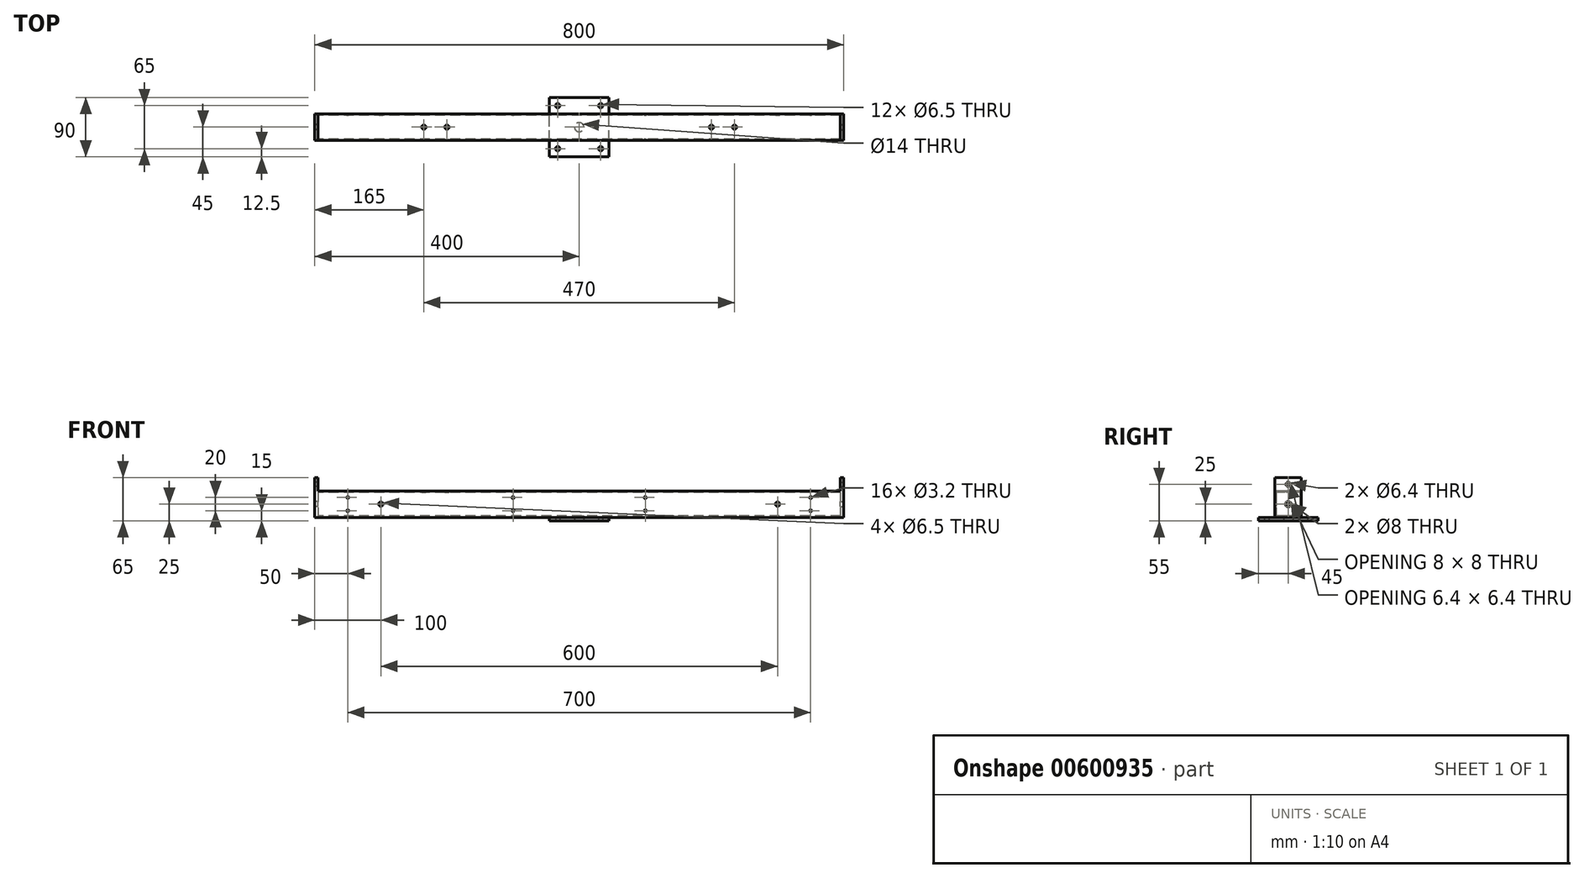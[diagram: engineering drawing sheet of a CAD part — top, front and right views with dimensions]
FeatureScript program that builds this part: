
annotation { "Feature Type Name" : "Feature", "Feature Type Description" : "" }
export const myFeature = defineFeature(function(context is Context, id is Id, definition is map)
    precondition{}
    {
        {
            var Q0;
            Q0=qCreatedBy(makeId("Right.planeOp"),FACE);
            var sketch = newSketch(context, id + "F0", { "sketchPlane" : qUnion([Q0])});
            skLineSegment(sketch, "E0.bottom", {"start": v(20, 20) * mm, "end": v(-20, 20) * mm});
            skLineSegment(sketch, "E0.top", {"start": v(20, -20) * mm, "end": v(-20, -20) * mm});
            skLineSegment(sketch, "E0.left", {"start": v(20, 20) * mm, "end": v(20, -20) * mm});
            skLineSegment(sketch, "E0.right", {"start": v(-20, 20) * mm, "end": v(-20, -20) * mm});
            skPoint(sketch, "E0.middle", {"position": v(0, 0) * mm});
            skLineSegment(sketch, "E1.bottom", {"start": v(18, 18) * mm, "end": v(-18, 18) * mm});
            skLineSegment(sketch, "E1.top", {"start": v(18, -18) * mm, "end": v(-18, -18) * mm});
            skLineSegment(sketch, "E1.left", {"start": v(18, 18) * mm, "end": v(18, -18) * mm});
            skLineSegment(sketch, "E1.right", {"start": v(-18, 18) * mm, "end": v(-18, -18) * mm});
            skSolve(sketch);
        }
        {
            var Q0;
            Q0=makeQuery(id+"F0.imprint","IMPRINT",FACE,{"disambiguationData":[TD([[makeQuery(id+"F0.imprint","IMPRINT",EDGE,{"derivedFrom":sQuery(id+"F0.wireOp",EDGE,"E0.bottom")}),1.0]])]});
            extrude(context, id + "F1", {"entities" : qUnion([Q0]), "depth" : 400 * mm, "offsetDistance" : 25 * mm});
        }
        {
            var Q0;
            Q0=qCreatedBy(makeId("Right.planeOp"),FACE);
            var sketch = newSketch(context, id + "F2", { "sketchPlane" : qUnion([Q0])});
            skLineSegment(sketch, "E2.bottom", {"start": v(20, -20) * mm, "end": v(-20, -20) * mm});
            skLineSegment(sketch, "E2.top", {"start": v(20, 40) * mm, "end": v(-20, 40) * mm});
            skLineSegment(sketch, "E2.left", {"start": v(20, -20) * mm, "end": v(20, 40) * mm});
            skLineSegment(sketch, "E2.right", {"start": v(-20, -20) * mm, "end": v(-20, 40) * mm});
            skPoint(sketch, "E3", {"position": v(0, 30) * mm});
            skPoint(sketch, "E4", {"position": v(0, 0) * mm});
            skSolve(sketch);
        }
        {
            var Q0;
            Q0=makeQuery(id+"F2.imprint","IMPRINT",FACE,{"disambiguationData":[TD([[makeQuery(id+"F2.imprint","IMPRINT",EDGE,{"derivedFrom":sQuery(id+"F2.wireOp",EDGE,"E2.bottom")}),-1.0]])]});
            extrude(context, id + "F3", {"entities" : qUnion([Q0]), "operationType" : NewBodyOperationType.ADD, "depth" : 5 * mm, "offsetDistance" : 25 * mm});
        }
        {
            var Q0;
            Q0=sQuery(id+"F2.wireOp",VERTEX,"E3");
            var Q1;
            Q1=makeQuery(id+"F1.opExtrude","SWEPT_BODY",BODY,{"disambiguationData":[OSD([sQuery(id+"F0.wireOp",EDGE,"E0.bottom"),sQuery(id+"F0.wireOp",EDGE,"E0.top"),sQuery(id+"F0.wireOp",EDGE,"E0.left"),sQuery(id+"F0.wireOp",EDGE,"E0.right"),sQuery(id+"F0.wireOp",EDGE,"E1.bottom"),sQuery(id+"F0.wireOp",EDGE,"E1.top"),sQuery(id+"F0.wireOp",EDGE,"E1.left"),sQuery(id+"F0.wireOp",EDGE,"E1.right")])]});
            hole(context, id + "F4", {"style" : HoleStyle.SIMPLE, "endStyle" : HoleEndStyle.THROUGH, "oppositeDirection" : true, "standardTappedOrClearance" : lookupTablePath({ "standard" : "ISO", "size" : "6.4", "type" : "Drilled" }), "standardBlindInLast" : lookupTablePath({ "standard" : "ISO", "size" : "6.4", "type" : "Drilled" }), "holeDiameter" : 6.4 * mm, "isTappedThrough" : true, "tappedDepth" : 3.5 * mm, "tapClearance" : 3, "locations" : qUnion([Q0]), "scope" : qUnion([Q1])});
        }
        {
            var Q0;
            Q0=makeQuery(id+"F1.opExtrude","SWEPT_FACE",FACE,{"disambiguationData":[OSD([sQuery(id+"F0.wireOp",EDGE,"E0.bottom")])]});
            var sketch = newSketch(context, id + "F5", { "sketchPlane" : qUnion([Q0])});
            skPoint(sketch, "E5", {"position": v(200, 0) * mm});
            skPoint(sketch, "E6", {"position": v(165, 0) * mm});
            skSolve(sketch);
        }
        {
            var Q0;
            Q0=sQuery(id+"F5.wireOp",VERTEX,"E6");
            var Q1;
            Q1=sQuery(id+"F5.wireOp",VERTEX,"E5");
            var Q2;
            Q2=makeQuery(id+"F1.opExtrude","SWEPT_BODY",BODY,{"disambiguationData":[OSD([sQuery(id+"F0.wireOp",EDGE,"E0.bottom"),sQuery(id+"F0.wireOp",EDGE,"E0.top"),sQuery(id+"F0.wireOp",EDGE,"E0.left"),sQuery(id+"F0.wireOp",EDGE,"E0.right"),sQuery(id+"F0.wireOp",EDGE,"E1.bottom"),sQuery(id+"F0.wireOp",EDGE,"E1.top"),sQuery(id+"F0.wireOp",EDGE,"E1.left"),sQuery(id+"F0.wireOp",EDGE,"E1.right")])]});
            hole(context, id + "F6", {"style" : HoleStyle.SIMPLE, "endStyle" : HoleEndStyle.THROUGH, "standardTappedOrClearance" : lookupTablePath({ "standard" : "ISO", "size" : "6.5", "type" : "Drilled" }), "standardBlindInLast" : lookupTablePath({ "standard" : "ISO", "size" : "6.5", "type" : "Drilled" }), "holeDiameter" : 6.5 * mm, "isTappedThrough" : true, "tappedDepth" : 3.5 * mm, "tapClearance" : 3, "locations" : qUnion([Q0, Q1]), "scope" : qUnion([Q2])});
        }
        {
            var Q0;
            Q0=makeQuery(id+"F3.boolean.opBoolean","MERGE",FACE,{"derivedFrom":[makeQuery(id+"F1.opExtrude","SWEPT_FACE",FACE,{"disambiguationData":[OSD([sQuery(id+"F0.wireOp",EDGE,"E0.right")])]}),makeQuery(id+"F3.opExtrude","SWEPT_FACE",FACE,{"disambiguationData":[OSD([sQuery(id+"F2.wireOp",EDGE,"E2.right")])]})]});
            var sketch = newSketch(context, id + "F7", { "sketchPlane" : qUnion([Q0])});
            skPoint(sketch, "E7", {"position": v(50, 10) * mm});
            skPoint(sketch, "E8", {"position": v(50, -10) * mm});
            skPoint(sketch, "E9", {"position": v(300, 10) * mm});
            skPoint(sketch, "E10", {"position": v(300, -10) * mm});
            skPoint(sketch, "E11", {"position": v(100, 0) * mm});
            skSolve(sketch);
        }
        {
            var Q0;
            Q0=sQuery(id+"F7.wireOp",VERTEX,"E7");
            var Q1;
            Q1=sQuery(id+"F7.wireOp",VERTEX,"E8");
            var Q2;
            Q2=sQuery(id+"F7.wireOp",VERTEX,"E9");
            var Q3;
            Q3=sQuery(id+"F7.wireOp",VERTEX,"E10");
            var Q4;
            Q4=makeQuery(id+"F1.opExtrude","SWEPT_BODY",BODY,{"disambiguationData":[OSD([sQuery(id+"F0.wireOp",EDGE,"E0.bottom"),sQuery(id+"F0.wireOp",EDGE,"E0.top"),sQuery(id+"F0.wireOp",EDGE,"E0.left"),sQuery(id+"F0.wireOp",EDGE,"E0.right"),sQuery(id+"F0.wireOp",EDGE,"E1.bottom"),sQuery(id+"F0.wireOp",EDGE,"E1.top"),sQuery(id+"F0.wireOp",EDGE,"E1.left"),sQuery(id+"F0.wireOp",EDGE,"E1.right")])]});
            hole(context, id + "F8", {"style" : HoleStyle.SIMPLE, "endStyle" : HoleEndStyle.THROUGH, "standardTappedOrClearance" : lookupTablePath({ "standard" : "ISO", "size" : "3.2", "type" : "Drilled" }), "standardBlindInLast" : lookupTablePath({ "standard" : "ISO", "size" : "3.2", "type" : "Drilled" }), "holeDiameter" : 3.2 * mm, "isTappedThrough" : true, "tappedDepth" : 3.5 * mm, "tapClearance" : 3, "locations" : qUnion([Q0, Q1, Q2, Q3]), "scope" : qUnion([Q4])});
        }
        {
            var Q0;
            Q0=sQuery(id+"F2.wireOp",VERTEX,"E4");
            var Q1;
            Q1=makeQuery(id+"F1.opExtrude","SWEPT_BODY",BODY,{"disambiguationData":[OSD([sQuery(id+"F0.wireOp",EDGE,"E0.bottom"),sQuery(id+"F0.wireOp",EDGE,"E0.top"),sQuery(id+"F0.wireOp",EDGE,"E0.left"),sQuery(id+"F0.wireOp",EDGE,"E0.right"),sQuery(id+"F0.wireOp",EDGE,"E1.bottom"),sQuery(id+"F0.wireOp",EDGE,"E1.top"),sQuery(id+"F0.wireOp",EDGE,"E1.left"),sQuery(id+"F0.wireOp",EDGE,"E1.right")])]});
            hole(context, id + "F9", {"style" : HoleStyle.SIMPLE, "endStyle" : HoleEndStyle.THROUGH, "oppositeDirection" : true, "standardTappedOrClearance" : lookupTablePath({ "standard" : "ISO", "size" : "8", "type" : "Drilled" }), "standardBlindInLast" : lookupTablePath({ "standard" : "ISO", "size" : "8", "type" : "Drilled" }), "holeDiameter" : 8 * mm, "isTappedThrough" : true, "tappedDepth" : 3.5 * mm, "tapClearance" : 3, "locations" : qUnion([Q0]), "scope" : qUnion([Q1])});
        }
        {
            var Q0;
            Q0=sQuery(id+"F7.wireOp",VERTEX,"E11");
            var Q1;
            Q1=makeQuery(id+"F1.opExtrude","SWEPT_BODY",BODY,{"disambiguationData":[OSD([sQuery(id+"F0.wireOp",EDGE,"E0.bottom"),sQuery(id+"F0.wireOp",EDGE,"E0.top"),sQuery(id+"F0.wireOp",EDGE,"E0.left"),sQuery(id+"F0.wireOp",EDGE,"E0.right"),sQuery(id+"F0.wireOp",EDGE,"E1.bottom"),sQuery(id+"F0.wireOp",EDGE,"E1.top"),sQuery(id+"F0.wireOp",EDGE,"E1.left"),sQuery(id+"F0.wireOp",EDGE,"E1.right")])]});
            hole(context, id + "F10", {"style" : HoleStyle.SIMPLE, "endStyle" : HoleEndStyle.THROUGH, "standardTappedOrClearance" : lookupTablePath({ "standard" : "ISO", "size" : "6.5", "type" : "Drilled" }), "standardBlindInLast" : lookupTablePath({ "standard" : "ISO", "size" : "6.5", "type" : "Drilled" }), "holeDiameter" : 6.5 * mm, "isTappedThrough" : true, "tappedDepth" : 3.5 * mm, "tapClearance" : 3, "locations" : qUnion([Q0]), "scope" : qUnion([Q1])});
        }
        {
            var Q0;
            Q0=makeQuery(id+"F1.opExtrude","CAP_FACE",FACE,{"disambiguationData":[OSD([sQuery(id+"F0.wireOp",EDGE,"E0.bottom"),sQuery(id+"F0.wireOp",EDGE,"E0.top"),sQuery(id+"F0.wireOp",EDGE,"E0.left"),sQuery(id+"F0.wireOp",EDGE,"E0.right"),sQuery(id+"F0.wireOp",EDGE,"E1.bottom"),sQuery(id+"F0.wireOp",EDGE,"E1.top"),sQuery(id+"F0.wireOp",EDGE,"E1.left"),sQuery(id+"F0.wireOp",EDGE,"E1.right")])],"isStart":false});
            var sketch = newSketch(context, id + "F11", { "sketchPlane" : qUnion([Q0])});
            skSolve(sketch);
        }
        {
            var Q0;
            Q0=makeQuery(id+"F1.opExtrude","SWEPT_BODY",BODY,{"disambiguationData":[OSD([sQuery(id+"F0.wireOp",EDGE,"E0.bottom"),sQuery(id+"F0.wireOp",EDGE,"E0.top"),sQuery(id+"F0.wireOp",EDGE,"E0.left"),sQuery(id+"F0.wireOp",EDGE,"E0.right"),sQuery(id+"F0.wireOp",EDGE,"E1.bottom"),sQuery(id+"F0.wireOp",EDGE,"E1.top"),sQuery(id+"F0.wireOp",EDGE,"E1.left"),sQuery(id+"F0.wireOp",EDGE,"E1.right")])]});
            var Q1;
            Q1=makeQuery(id+"F11.imprint","IMPRINT",FACE,{"disambiguationData":[TD([[makeQuery(id+"F11.imprint","IMPRINT",EDGE,{"derivedFrom":makeQuery(id+"F1.opExtrude","CAP_EDGE",EDGE,{"disambiguationData":[OSD([sQuery(id+"F0.wireOp",EDGE,"E0.bottom")])],"isStart":false})}),1.0]])]});
            mirror(context, id + "F12", {"operationType" : NewBodyOperationType.ADD, "entities" : qUnion([Q0]), "mirrorPlane" : qUnion([Q1])});
        }
        {
            var Q0;
            {var subQ0=makeQuery(id+"F1.opExtrude","SWEPT_FACE",FACE,{"disambiguationData":[OSD([sQuery(id+"F0.wireOp",EDGE,"E0.top")])]});Q0=makeQuery(id+"F12.boolean.opBoolean","MERGE",FACE,{"derivedFrom":[subQ0,makeQuery(id+"F12.opPattern","COPY",FACE,{"derivedFrom":subQ0,"instanceName":"1"})]});}
            var sketch = newSketch(context, id + "F13", { "sketchPlane" : qUnion([Q0])});
            skLineSegment(sketch, "E12.bottom", {"start": v(355, 45) * mm, "end": v(445, 45) * mm});
            skLineSegment(sketch, "E12.top", {"start": v(355, -45) * mm, "end": v(445, -45) * mm});
            skLineSegment(sketch, "E12.left", {"start": v(355, 45) * mm, "end": v(355, -45) * mm});
            skLineSegment(sketch, "E12.right", {"start": v(445, 45) * mm, "end": v(445, -45) * mm});
            skSolve(sketch);
        }
        {
            var Q0;
            {var subQ0=sQuery(id+"F13.wireOp",EDGE,"E12.bottom");Q0=makeQuery(id+"F13.imprint","IMPRINT",FACE,{"disambiguationData":[TD([[makeQuery(id+"F13.imprint","IMPRINT",EDGE,{"derivedFrom":subQ0}),-1.0]])]});}
            var Q1;
            {var subQ0=sQuery(id+"F13.wireOp",EDGE,"E12.top");Q1=makeQuery(id+"F13.imprint","IMPRINT",FACE,{"disambiguationData":[TD([[makeQuery(id+"F13.imprint","IMPRINT",EDGE,{"derivedFrom":subQ0}),1.0]])]});}
            var Q2;
            {var subQ0=sQuery(id+"F13.wireOp",EDGE,"E12.left");var subQ1=sQuery(id+"F0.wireOp",EDGE,"E0.top");var subQ2=makeQuery(id+"F1.opExtrude","SWEPT_EDGE",EDGE,{"disambiguationData":[OSD([subQ1,sQuery(id+"F0.wireOp",EDGE,"E0.right")])]});var subQ3=makeQuery(id+"F12.boolean.opBoolean","MERGE",EDGE,{"derivedFrom":[subQ2,makeQuery(id+"F12.opPattern","COPY",EDGE,{"derivedFrom":subQ2,"instanceName":"1"})]});var subQ4=makeQuery(id+"F13.imprint","INTERSECT",VERTEX,{"derivedFrom":[subQ3,subQ0]});Q2=makeQuery(id+"F13.imprint","IMPRINT",FACE,{"disambiguationData":[TD([[makeQuery(id+"F13.imprint","IMPRINT",EDGE,{"disambiguationData":[TD([[subQ4,-1.0]])],"derivedFrom":subQ0}),1.0]])]});}
            extrude(context, id + "F14", {"entities" : qUnion([Q0, Q1, Q2]), "operationType" : NewBodyOperationType.ADD, "depth" : 5 * mm, "offsetDistance" : 25 * mm});
        }
        {
            var Q0;
            Q0=makeQuery(id+"F14.opExtrude","CAP_FACE",FACE,{"disambiguationData":[OSD([sQuery(id+"F13.wireOp",EDGE,"E12.bottom"),sQuery(id+"F13.wireOp",EDGE,"E12.top"),sQuery(id+"F13.wireOp",EDGE,"E12.left"),sQuery(id+"F13.wireOp",EDGE,"E12.right")])],"isStart":false});
            var sketch = newSketch(context, id + "F15", { "sketchPlane" : qUnion([Q0])});
            skPoint(sketch, "E13", {"position": v(367.5, 32.5) * mm});
            skPoint(sketch, "E14", {"position": v(432.5, 32.5) * mm});
            skPoint(sketch, "E15", {"position": v(432.5, -32.5) * mm});
            skPoint(sketch, "E16", {"position": v(367.5, -32.5) * mm});
            skPoint(sketch, "E17", {"position": v(400, 0) * mm});
            skSolve(sketch);
        }
        {
            var Q0;
            Q0=sQuery(id+"F15.wireOp",VERTEX,"E13");
            var Q1;
            Q1=sQuery(id+"F15.wireOp",VERTEX,"E14");
            var Q2;
            Q2=sQuery(id+"F15.wireOp",VERTEX,"E15");
            var Q3;
            Q3=sQuery(id+"F15.wireOp",VERTEX,"E16");
            var Q4;
            Q4=makeQuery(id+"F1.opExtrude","SWEPT_BODY",BODY,{"disambiguationData":[OSD([sQuery(id+"F0.wireOp",EDGE,"E0.bottom"),sQuery(id+"F0.wireOp",EDGE,"E0.top"),sQuery(id+"F0.wireOp",EDGE,"E0.left"),sQuery(id+"F0.wireOp",EDGE,"E0.right"),sQuery(id+"F0.wireOp",EDGE,"E1.bottom"),sQuery(id+"F0.wireOp",EDGE,"E1.top"),sQuery(id+"F0.wireOp",EDGE,"E1.left"),sQuery(id+"F0.wireOp",EDGE,"E1.right")])]});
            hole(context, id + "F16", {"style" : HoleStyle.SIMPLE, "endStyle" : HoleEndStyle.THROUGH, "standardTappedOrClearance" : lookupTablePath({ "standard" : "ISO", "size" : "6.5", "type" : "Drilled" }), "standardBlindInLast" : lookupTablePath({ "standard" : "ISO", "size" : "6.5", "type" : "Drilled" }), "holeDiameter" : 6.5 * mm, "isTappedThrough" : true, "tappedDepth" : 3.5 * mm, "tapClearance" : 3, "locations" : qUnion([Q0, Q1, Q2, Q3]), "scope" : qUnion([Q4])});
        }
        {
            var Q0;
            Q0=sQuery(id+"F15.wireOp",VERTEX,"E17");
            var Q1;
            Q1=makeQuery(id+"F1.opExtrude","SWEPT_BODY",BODY,{"disambiguationData":[OSD([sQuery(id+"F0.wireOp",EDGE,"E0.bottom"),sQuery(id+"F0.wireOp",EDGE,"E0.top"),sQuery(id+"F0.wireOp",EDGE,"E0.left"),sQuery(id+"F0.wireOp",EDGE,"E0.right"),sQuery(id+"F0.wireOp",EDGE,"E1.bottom"),sQuery(id+"F0.wireOp",EDGE,"E1.top"),sQuery(id+"F0.wireOp",EDGE,"E1.left"),sQuery(id+"F0.wireOp",EDGE,"E1.right")])]});
            hole(context, id + "F17", {"style" : HoleStyle.SIMPLE, "endStyle" : HoleEndStyle.BLIND, "standardTappedOrClearance" : lookupTablePath({ "standard" : "ISO", "size" : "14", "type" : "Drilled" }), "standardBlindInLast" : lookupTablePath({ "standard" : "ISO", "size" : "14", "type" : "Drilled" }), "holeDiameter" : 14 * mm, "holeDepth" : 10 * mm, "isTappedThrough" : true, "tappedDepth" : 3.5 * mm, "tapClearance" : 3, "locations" : qUnion([Q0]), "scope" : qUnion([Q1])});
        }
    });
